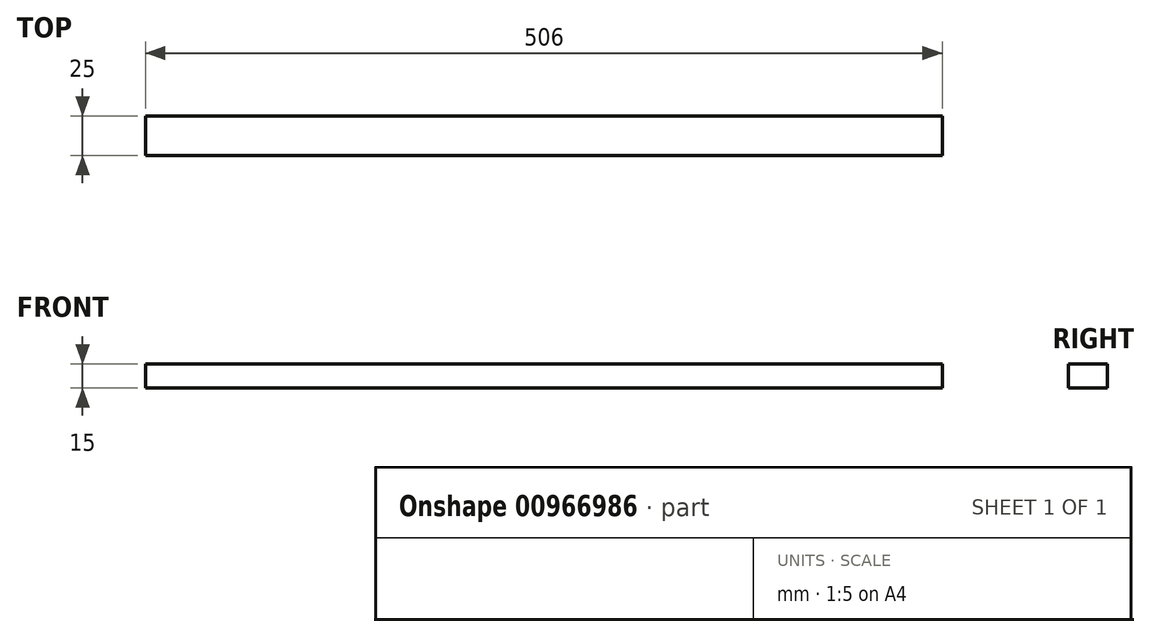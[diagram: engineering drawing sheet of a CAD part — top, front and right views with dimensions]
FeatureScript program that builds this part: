
annotation { "Feature Type Name" : "Feature", "Feature Type Description" : "" }
export const myFeature = defineFeature(function(context is Context, id is Id, definition is map)
    precondition{}
    {
        {
            var Q0;
            Q0=qCreatedBy(makeId("Front.planeOp"),FACE);
            var sketch = newSketch(context, id + "F0", { "sketchPlane" : qUnion([Q0])});
            skLineSegment(sketch, "E0.bottom", {"start": v(0, 0) * mm, "end": v(506, 0) * mm});
            skLineSegment(sketch, "E0.top", {"start": v(0, 15) * mm, "end": v(506, 15) * mm});
            skLineSegment(sketch, "E0.left", {"start": v(0, 0) * mm, "end": v(0, 15) * mm});
            skLineSegment(sketch, "E0.right", {"start": v(506, 0) * mm, "end": v(506, 15) * mm});
            skSolve(sketch);
        }
        {
            var Q0;
            Q0 = qSketchRegion(id + "F0", true);
            extrude(context, id + "F1", {"entities" : qUnion([Q0]), "depth" : 25 * mm, "offsetDistance" : 25 * mm});
        }
    });
